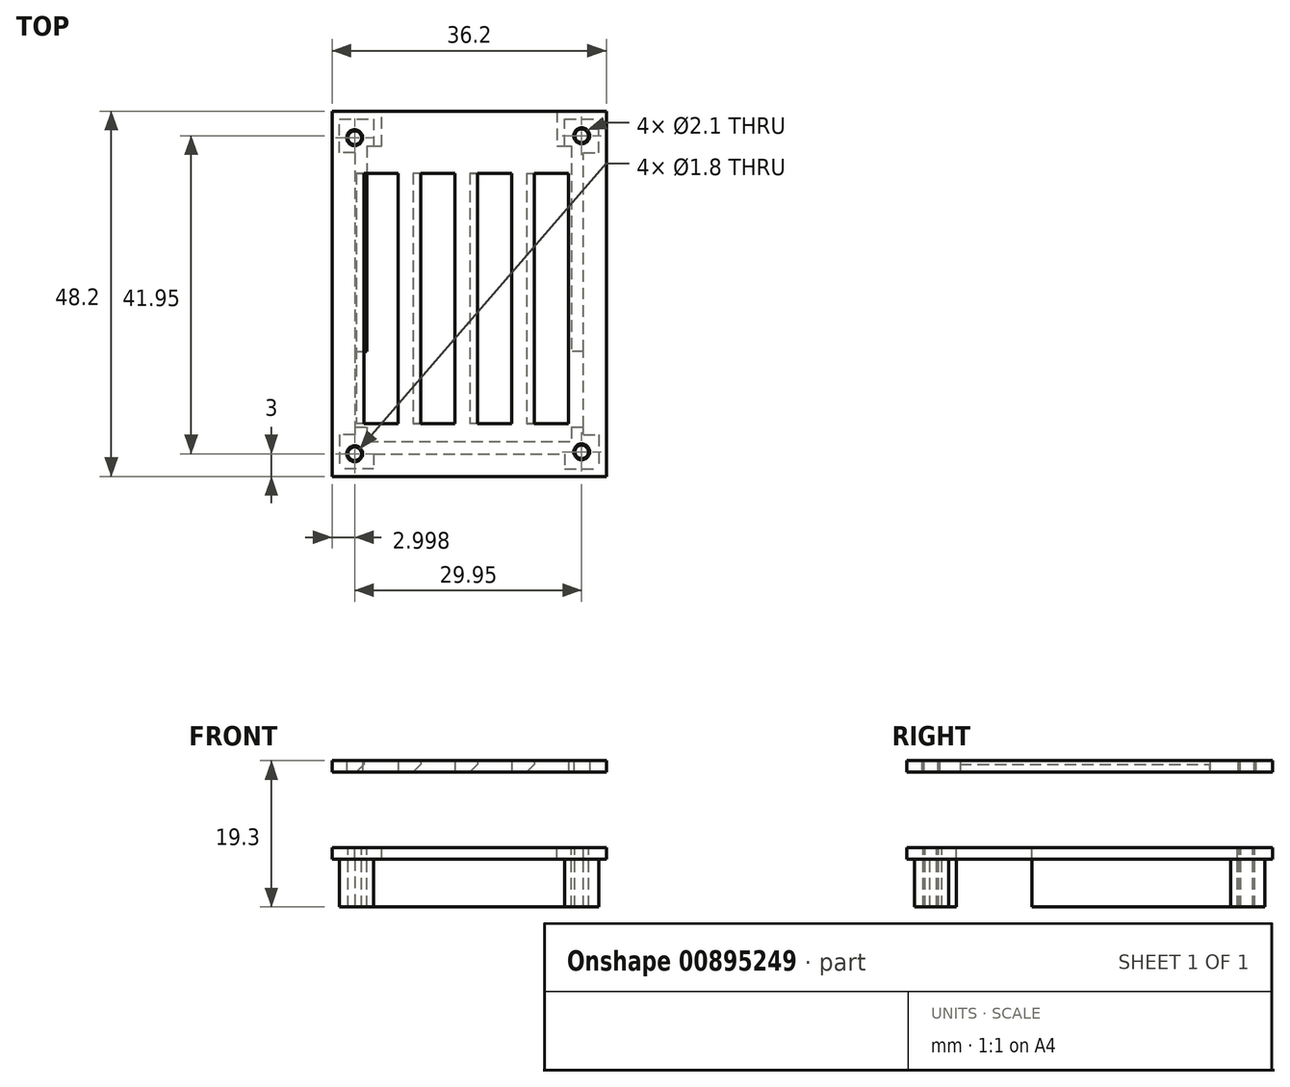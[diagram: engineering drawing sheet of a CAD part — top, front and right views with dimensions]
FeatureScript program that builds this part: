
annotation { "Feature Type Name" : "Feature", "Feature Type Description" : "" }
export const myFeature = defineFeature(function(context is Context, id is Id, definition is map)
    precondition{}
    {
        {
            var Q0;
            Q0=qCreatedBy(makeId("Top.planeOp"),FACE);
            var sketch = newSketch(context, id + "F0", { "sketchPlane" : qUnion([Q0])});
            skLineSegment(sketch, "E0.bottom", {"start": v(-14.17, 10.15) * mm, "end": v(12.83, 10.15) * mm});
            skLineSegment(sketch, "E0.top", {"start": v(-14.17, -28.85) * mm, "end": v(12.83, -28.85) * mm});
            skLineSegment(sketch, "E0.left", {"start": v(-14.17, 10.15) * mm, "end": v(-14.17, -28.85) * mm});
            skLineSegment(sketch, "E0.right", {"start": v(12.83, 10.15) * mm, "end": v(12.83, -28.85) * mm});
            skLineSegment(sketch, "E1.bottom", {"start": v(-12.17, 10.15) * mm, "end": v(-3.17, 10.15) * mm});
            skLineSegment(sketch, "E1.left", {"start": v(-12.17, 10.15) * mm, "end": v(-12.17, 14.75) * mm});
            skLineSegment(sketch, "E2", {"start": v(-15.77, 11.75) * mm, "end": v(-15.77, -30.45) * mm});
            skLineSegment(sketch, "E3", {"start": v(-15.77, -30.45) * mm, "end": v(14.43, -30.45) * mm});
            skLineSegment(sketch, "E4", {"start": v(14.43, -30.45) * mm, "end": v(14.43, 11.75) * mm});
            skLineSegment(sketch, "E5", {"start": v(14.43, 11.75) * mm, "end": v(10.93, 11.75) * mm});
            skLineSegment(sketch, "E6", {"start": v(-1.77, 31.75) * mm, "end": v(-3.27, 31.75) * mm});
            skLineSegment(sketch, "E7", {"start": v(-13.77, 14.75) * mm, "end": v(-13.77, 11.75) * mm});
            skLineSegment(sketch, "E8", {"start": v(-13.77, 11.75) * mm, "end": v(-15.77, 11.75) * mm});
            skLineSegment(sketch, "E9", {"start": v(-13.77, 14.75) * mm, "end": v(-18.77, 14.75) * mm});
            skLineSegment(sketch, "E10", {"start": v(-18.77, 14.75) * mm, "end": v(-18.77, -33.45) * mm});
            skLineSegment(sketch, "E11", {"start": v(-18.77, -33.45) * mm, "end": v(17.43, -33.45) * mm});
            skLineSegment(sketch, "E12", {"start": v(17.43, -33.45) * mm, "end": v(17.43, 14.75) * mm});
            skLineSegment(sketch, "E13", {"start": v(17.43, 14.75) * mm, "end": v(10.93, 14.75) * mm});
            skLineSegment(sketch, "E14.bottom", {"start": v(11.93, 9.25) * mm, "end": v(16.43, 9.25) * mm});
            skLineSegment(sketch, "E14.top", {"start": v(11.93, 13.75) * mm, "end": v(16.43, 13.75) * mm});
            skLineSegment(sketch, "E14.left", {"start": v(11.93, 9.25) * mm, "end": v(11.93, 13.75) * mm});
            skLineSegment(sketch, "E14.right", {"start": v(16.43, 9.25) * mm, "end": v(16.43, 13.75) * mm});
            skLineSegment(sketch, "E15.bottom", {"start": v(-13.27, 9.25) * mm, "end": v(-17.77, 9.25) * mm});
            skLineSegment(sketch, "E15.top", {"start": v(-13.27, 13.75) * mm, "end": v(-17.77, 13.75) * mm});
            skLineSegment(sketch, "E15.left", {"start": v(-13.27, 9.25) * mm, "end": v(-13.27, 13.75) * mm});
            skLineSegment(sketch, "E15.right", {"start": v(-17.77, 9.25) * mm, "end": v(-17.77, 13.75) * mm});
            skLineSegment(sketch, "E16.bottom", {"start": v(-13.27, -27.95) * mm, "end": v(-17.77, -27.95) * mm});
            skLineSegment(sketch, "E16.top", {"start": v(-13.27, -32.45) * mm, "end": v(-17.77, -32.45) * mm});
            skLineSegment(sketch, "E16.left", {"start": v(-13.27, -27.95) * mm, "end": v(-13.27, -32.45) * mm});
            skLineSegment(sketch, "E16.right", {"start": v(-17.77, -27.95) * mm, "end": v(-17.77, -32.45) * mm});
            skLineSegment(sketch, "E17.bottom", {"start": v(11.93, -27.95) * mm, "end": v(16.43, -27.95) * mm});
            skLineSegment(sketch, "E17.top", {"start": v(11.93, -32.45) * mm, "end": v(16.43, -32.45) * mm});
            skLineSegment(sketch, "E17.left", {"start": v(11.93, -27.95) * mm, "end": v(11.93, -32.45) * mm});
            skLineSegment(sketch, "E17.right", {"start": v(16.43, -27.95) * mm, "end": v(16.43, -32.45) * mm});
            skCircle(sketch, "E18", {"center": v(14.18, 11.5) * mm, "radius": 2.25 * mm});
            skPoint(sketch, "E18.centerSnap0", {"position": v(16.43, 11.5) * mm});
            skCircle(sketch, "E19", {"center": v(-15.77, 11.25) * mm, "radius": 2 * mm});
            skCircle(sketch, "E20", {"center": v(-15.77, -30.45) * mm, "radius": 2 * mm});
            skCircle(sketch, "E21", {"center": v(14.18, -30.2) * mm, "radius": 2.25 * mm});
            skLineSegment(sketch, "E22", {"start": v(-12.17, 30.25) * mm, "end": v(-12.17, 31.75) * mm});
            skLineSegment(sketch, "E23", {"start": v(-3.27, 30.25) * mm, "end": v(-3.27, 31.75) * mm});
            skLineSegment(sketch, "E24.trimOffspring", {"start": v(-12.17, 31.75) * mm, "end": v(-13.77, 31.75) * mm});
            skLineSegment(sketch, "E25", {"start": v(-13.77, 14.75) * mm, "end": v(-12.17, 14.75) * mm});
            skLineSegment(sketch, "E26", {"start": v(10.93, 14.75) * mm, "end": v(10.93, 10.15) * mm});
            skLineSegment(sketch, "E27", {"start": v(14.43, -16.95) * mm, "end": v(12.83, -16.95) * mm});
            skLineSegment(sketch, "E28", {"start": v(-13.27, 13.75) * mm, "end": v(-13.27, 14.75) * mm});
            skLineSegment(sketch, "E29", {"start": v(-15.77, -16.95) * mm, "end": v(-14.17, -16.95) * mm});
            skLineSegment(sketch, "E30", {"start": v(-15.77, -26.95) * mm, "end": v(-14.17, -26.95) * mm});
            skLineSegment(sketch, "E31", {"start": v(12.83, -26.95) * mm, "end": v(14.43, -26.95) * mm});
            skSolve(sketch);
        }
        {
            var Q0;
            Q0=makeQuery(id+"F0.imprint","IMPRINT",FACE,{"disambiguationData":[TD([[makeQuery(id+"F0.imprint","IMPRINT",EDGE,{"derivedFrom":sQuery(id+"F0.wireOp",EDGE,"E0.top")}),-1.0]])]});
            var Q1;
            {var subQ5=sQuery(id+"F0.wireOp",EDGE,"E0.left");var subQ6=sQuery(id+"F0.wireOp",EDGE,"E0.top");var subQ7=makeQuery(id+"F0.imprint","INTERSECT",VERTEX,{"derivedFrom":[subQ6,subQ5]});Q1=makeQuery(id+"F0.imprint","IMPRINT",FACE,{"disambiguationData":[TD([[makeQuery(id+"F0.imprint","IMPRINT",EDGE,{"disambiguationData":[TD([[subQ7,-1.0]])],"derivedFrom":subQ6}),-1.0]])]});}
            var Q2;
            {var subQ5=sQuery(id+"F0.wireOp",EDGE,"E0.right");var subQ6=sQuery(id+"F0.wireOp",EDGE,"E0.top");var subQ7=makeQuery(id+"F0.imprint","INTERSECT",VERTEX,{"derivedFrom":[subQ6,subQ5]});Q2=makeQuery(id+"F0.imprint","IMPRINT",FACE,{"disambiguationData":[TD([[makeQuery(id+"F0.imprint","IMPRINT",EDGE,{"disambiguationData":[TD([[subQ7,1.0]])],"derivedFrom":subQ6}),-1.0]])]});}
            var Q3;
            {var subQ0=sQuery(id+"F0.wireOp",EDGE,"E14.bottom");var subQ1=sQuery(id+"F0.wireOp",EDGE,"E0.right");var subQ2=makeQuery(id+"F0.imprint","INTERSECT",VERTEX,{"derivedFrom":[subQ1,subQ0]});Q3=makeQuery(id+"F0.imprint","IMPRINT",FACE,{"disambiguationData":[TD([[makeQuery(id+"F0.imprint","IMPRINT",EDGE,{"disambiguationData":[TD([[subQ2,-1.0]])],"derivedFrom":subQ1}),1.0]])]});}
            var Q4;
            {var subQ7=sQuery(id+"F0.wireOp",EDGE,"E0.right");var subQ8=sQuery(id+"F0.wireOp",EDGE,"E0.bottom");var subQ9=makeQuery(id+"F0.imprint","INTERSECT",VERTEX,{"derivedFrom":[subQ8,subQ7]});Q4=makeQuery(id+"F0.imprint","IMPRINT",FACE,{"disambiguationData":[TD([[makeQuery(id+"F0.imprint","IMPRINT",EDGE,{"disambiguationData":[TD([[subQ9,1.0]])],"derivedFrom":subQ8}),1.0]])]});}
            var Q5;
            {var subQ0=sQuery(id+"F0.wireOp",EDGE,"E15.bottom");var subQ1=sQuery(id+"F0.wireOp",EDGE,"E0.left");var subQ2=makeQuery(id+"F0.imprint","INTERSECT",VERTEX,{"derivedFrom":[subQ1,subQ0]});Q5=makeQuery(id+"F0.imprint","IMPRINT",FACE,{"disambiguationData":[TD([[makeQuery(id+"F0.imprint","IMPRINT",EDGE,{"disambiguationData":[TD([[subQ2,-1.0]])],"derivedFrom":subQ1}),-1.0]])]});}
            var Q6;
            {var subQ0=sQuery(id+"F0.wireOp",EDGE,"E16.bottom");var subQ1=sQuery(id+"F0.wireOp",EDGE,"E0.left");var subQ2=makeQuery(id+"F0.imprint","INTERSECT",VERTEX,{"derivedFrom":[subQ1,subQ0]});Q6=makeQuery(id+"F0.imprint","IMPRINT",FACE,{"disambiguationData":[TD([[makeQuery(id+"F0.imprint","IMPRINT",EDGE,{"disambiguationData":[TD([[subQ2,-1.0]])],"derivedFrom":subQ1}),-1.0]])]});}
            var Q7;
            {var subQ0=sQuery(id+"F0.wireOp",EDGE,"E20");var subQ1=sQuery(id+"F0.wireOp",EDGE,"E3");var subQ2=makeQuery(id+"F0.imprint","INTERSECT",VERTEX,{"derivedFrom":[subQ1,subQ0]});Q7=makeQuery(id+"F0.imprint","IMPRINT",FACE,{"disambiguationData":[TD([[makeQuery(id+"F0.imprint","IMPRINT",EDGE,{"disambiguationData":[TD([[subQ2,-1.0]])],"derivedFrom":subQ1}),1.0]])]});}
            var Q8;
            {var subQ0=sQuery(id+"F0.wireOp",EDGE,"E16.left");var subQ1=sQuery(id+"F0.wireOp",EDGE,"E0.top");var subQ2=makeQuery(id+"F0.imprint","INTERSECT",VERTEX,{"derivedFrom":[subQ1,subQ0]});Q8=makeQuery(id+"F0.imprint","IMPRINT",FACE,{"disambiguationData":[TD([[makeQuery(id+"F0.imprint","IMPRINT",EDGE,{"disambiguationData":[TD([[subQ2,-1.0]])],"derivedFrom":subQ1}),-1.0]])]});}
            var Q9;
            {var subQ0=sQuery(id+"F0.wireOp",EDGE,"E16.bottom");var subQ1=sQuery(id+"F0.wireOp",EDGE,"E2");var subQ2=makeQuery(id+"F0.imprint","INTERSECT",VERTEX,{"derivedFrom":[subQ1,subQ0]});Q9=makeQuery(id+"F0.imprint","IMPRINT",FACE,{"disambiguationData":[TD([[makeQuery(id+"F0.imprint","IMPRINT",EDGE,{"disambiguationData":[TD([[subQ2,-1.0]])],"derivedFrom":subQ1}),1.0]])]});}
            var Q10;
            {var subQ0=sQuery(id+"F0.wireOp",EDGE,"E17.bottom");var subQ1=sQuery(id+"F0.wireOp",EDGE,"E0.right");var subQ2=makeQuery(id+"F0.imprint","INTERSECT",VERTEX,{"derivedFrom":[subQ1,subQ0]});Q10=makeQuery(id+"F0.imprint","IMPRINT",FACE,{"disambiguationData":[TD([[makeQuery(id+"F0.imprint","IMPRINT",EDGE,{"disambiguationData":[TD([[subQ2,-1.0]])],"derivedFrom":subQ1}),1.0]])]});}
            var Q11;
            {var subQ0=sQuery(id+"F0.wireOp",EDGE,"E17.left");var subQ1=sQuery(id+"F0.wireOp",EDGE,"E3");var subQ2=makeQuery(id+"F0.imprint","INTERSECT",VERTEX,{"derivedFrom":[subQ1,subQ0]});Q11=makeQuery(id+"F0.imprint","IMPRINT",FACE,{"disambiguationData":[TD([[makeQuery(id+"F0.imprint","IMPRINT",EDGE,{"disambiguationData":[TD([[subQ2,-1.0]])],"derivedFrom":subQ1}),1.0]])]});}
            var Q12;
            {var subQ0=sQuery(id+"F0.wireOp",EDGE,"E21");var subQ1=sQuery(id+"F0.wireOp",EDGE,"E4");var subQ2=makeQuery(id+"F0.imprint","INTERSECT",VERTEX,{"derivedFrom":[subQ1,subQ0]});Q12=makeQuery(id+"F0.imprint","IMPRINT",FACE,{"disambiguationData":[TD([[makeQuery(id+"F0.imprint","IMPRINT",EDGE,{"disambiguationData":[TD([[subQ2,-1.0]])],"derivedFrom":subQ1}),1.0]])]});}
            var Q13;
            {var subQ0=sQuery(id+"F0.wireOp",EDGE,"E14.left");var subQ1=sQuery(id+"F0.wireOp",EDGE,"E0.bottom");var subQ2=makeQuery(id+"F0.imprint","INTERSECT",VERTEX,{"derivedFrom":[subQ1,subQ0]});Q13=makeQuery(id+"F0.imprint","IMPRINT",FACE,{"disambiguationData":[TD([[makeQuery(id+"F0.imprint","IMPRINT",EDGE,{"disambiguationData":[TD([[subQ2,-1.0]])],"derivedFrom":subQ1}),1.0]])]});}
            var Q14;
            {var subQ0=sQuery(id+"F0.wireOp",EDGE,"E18");var subQ1=sQuery(id+"F0.wireOp",EDGE,"E5");var subQ2=makeQuery(id+"F0.imprint","INTERSECT",VERTEX,{"derivedFrom":[subQ1,subQ0]});Q14=makeQuery(id+"F0.imprint","IMPRINT",FACE,{"disambiguationData":[TD([[makeQuery(id+"F0.imprint","IMPRINT",EDGE,{"disambiguationData":[TD([[subQ2,-1.0]])],"derivedFrom":subQ1}),1.0]])]});}
            var Q15;
            {var subQ0=sQuery(id+"F0.wireOp",EDGE,"E14.bottom");var subQ1=sQuery(id+"F0.wireOp",EDGE,"E4");var subQ2=makeQuery(id+"F0.imprint","INTERSECT",VERTEX,{"derivedFrom":[subQ1,subQ0]});Q15=makeQuery(id+"F0.imprint","IMPRINT",FACE,{"disambiguationData":[TD([[makeQuery(id+"F0.imprint","IMPRINT",EDGE,{"disambiguationData":[TD([[subQ2,-1.0]])],"derivedFrom":subQ1}),1.0]])]});}
            var Q16;
            {var subQ0=sQuery(id+"F0.wireOp",EDGE,"E18");var subQ1=sQuery(id+"F0.wireOp",EDGE,"E0.right");var subQ2=makeQuery(id+"F0.imprint","INTERSECT",VERTEX,{"derivedFrom":[subQ1,subQ0]});Q16=makeQuery(id+"F0.imprint","IMPRINT",FACE,{"disambiguationData":[TD([[makeQuery(id+"F0.imprint","IMPRINT",EDGE,{"disambiguationData":[TD([[subQ2,-1.0]])],"derivedFrom":subQ1}),1.0]])]});}
            var Q17;
            {var subQ0=sQuery(id+"F0.wireOp",EDGE,"E15.top");var subQ1=sQuery(id+"F0.wireOp",EDGE,"E7");var subQ2=makeQuery(id+"F0.imprint","INTERSECT",VERTEX,{"derivedFrom":[subQ1,subQ0]});Q17=makeQuery(id+"F0.imprint","IMPRINT",FACE,{"disambiguationData":[TD([[makeQuery(id+"F0.imprint","IMPRINT",EDGE,{"disambiguationData":[TD([[subQ2,-1.0]])],"derivedFrom":subQ1}),1.0]])]});}
            var Q18;
            {var subQ0=sQuery(id+"F0.wireOp",EDGE,"E19");var subQ1=sQuery(id+"F0.wireOp",EDGE,"E2");var subQ2=makeQuery(id+"F0.imprint","INTERSECT",VERTEX,{"derivedFrom":[subQ1,subQ0]});Q18=makeQuery(id+"F0.imprint","IMPRINT",FACE,{"disambiguationData":[TD([[makeQuery(id+"F0.imprint","IMPRINT",EDGE,{"disambiguationData":[TD([[subQ2,-1.0]])],"derivedFrom":subQ1}),1.0]])]});}
            var Q19;
            {var subQ0=sQuery(id+"F0.wireOp",EDGE,"E19");var subQ1=sQuery(id+"F0.wireOp",EDGE,"E0.left");var subQ2=makeQuery(id+"F0.imprint","INTERSECT",VERTEX,{"derivedFrom":[subQ1,subQ0]});Q19=makeQuery(id+"F0.imprint","IMPRINT",FACE,{"disambiguationData":[TD([[makeQuery(id+"F0.imprint","IMPRINT",EDGE,{"disambiguationData":[TD([[subQ2,-1.0]])],"derivedFrom":subQ1}),-1.0]])]});}
            var Q20;
            {var subQ0=sQuery(id+"F0.wireOp",EDGE,"E19");var subQ1=sQuery(id+"F0.wireOp",EDGE,"E0.bottom");var subQ2=makeQuery(id+"F0.imprint","INTERSECT",VERTEX,{"derivedFrom":[subQ1,subQ0]});Q20=makeQuery(id+"F0.imprint","IMPRINT",FACE,{"disambiguationData":[TD([[makeQuery(id+"F0.imprint","IMPRINT",EDGE,{"disambiguationData":[TD([[subQ2,-1.0]])],"derivedFrom":subQ1}),1.0]])]});}
            var Q21;
            {var subQ0=sQuery(id+"F0.wireOp",EDGE,"E8");Q21=makeQuery(id+"F0.imprint","IMPRINT",FACE,{"disambiguationData":[TD([[makeQuery(id+"F0.imprint","IMPRINT",EDGE,{"derivedFrom":subQ0}),1.0]])]});}
            var Q22;
            {var subQ0=sQuery(id+"F0.wireOp",EDGE,"E3");var subQ1=sQuery(id+"F0.wireOp",EDGE,"E2");var subQ2=makeQuery(id+"F0.imprint","INTERSECT",VERTEX,{"derivedFrom":[subQ1,subQ0]});Q22=makeQuery(id+"F0.imprint","IMPRINT",FACE,{"disambiguationData":[TD([[makeQuery(id+"F0.imprint","IMPRINT",EDGE,{"disambiguationData":[TD([[subQ2,1.0]])],"derivedFrom":subQ1}),1.0]])]});}
            var Q23;
            {var subQ9=sQuery(id+"F0.wireOp",EDGE,"E1.right");Q23=makeQuery(id+"F0.imprint","IMPRINT",FACE,{"disambiguationData":[TD([[makeQuery(id+"F0.imprint","IMPRINT",EDGE,{"derivedFrom":subQ9}),-1.0]])]});}
            var Q24;
            {var subQ0=sQuery(id+"F0.wireOp",EDGE,"E30");Q24=makeQuery(id+"F0.imprint","IMPRINT",FACE,{"disambiguationData":[TD([[makeQuery(id+"F0.imprint","IMPRINT",EDGE,{"derivedFrom":subQ0}),-1.0]])]});}
            var Q25;
            {var subQ4=sQuery(id+"F0.wireOp",EDGE,"E31");Q25=makeQuery(id+"F0.imprint","IMPRINT",FACE,{"disambiguationData":[TD([[makeQuery(id+"F0.imprint","IMPRINT",EDGE,{"derivedFrom":subQ4}),-1.0]])]});}
            extrude(context, id + "F1", {"entities" : qUnion([Q0, Q1, Q2, Q3, Q4, Q5, Q6, Q7, Q8, Q9, Q10, Q11, Q12, Q13, Q14, Q15, Q16, Q17, Q18, Q19, Q20, Q21, Q22, Q23, Q24, Q25]), "oppositeDirection" : true, "depth" : 7.8 * mm, "offsetDistance" : 25 * mm});
        }
        {
            var Q0;
            {var subQ28=sQuery(id+"F0.wireOp",EDGE,"E9");Q0=makeQuery(id+"F0.imprint","IMPRINT",FACE,{"disambiguationData":[TD([[makeQuery(id+"F0.imprint","IMPRINT",EDGE,{"derivedFrom":subQ28}),1.0]])]});}
            var Q1;
            {var subQ5=sQuery(id+"F0.wireOp",EDGE,"E7");var subQ7=sQuery(id+"F0.wireOp",EDGE,"E8");var subQ8=makeQuery(id+"F0.imprint","INTERSECT",VERTEX,{"derivedFrom":[subQ5,subQ7]});Q1=makeQuery(id+"F0.imprint","IMPRINT",FACE,{"disambiguationData":[TD([[makeQuery(id+"F0.imprint","IMPRINT",EDGE,{"disambiguationData":[TD([[subQ8,1.0]])],"derivedFrom":subQ5}),-1.0]])]});}
            var Q2;
            {var subQ0=sQuery(id+"F0.wireOp",EDGE,"E8");var subQ1=sQuery(id+"F0.wireOp",EDGE,"E2");var subQ2=makeQuery(id+"F0.imprint","INTERSECT",VERTEX,{"derivedFrom":[subQ1,subQ0]});Q2=makeQuery(id+"F0.imprint","IMPRINT",FACE,{"disambiguationData":[TD([[makeQuery(id+"F0.imprint","IMPRINT",EDGE,{"disambiguationData":[TD([[subQ2,1.0]])],"derivedFrom":subQ0}),-1.0]])]});}
            var Q3;
            {var subQ0=sQuery(id+"F0.wireOp",EDGE,"E15.right");var subQ1=sQuery(id+"F0.wireOp",EDGE,"E15.bottom");var subQ2=makeQuery(id+"F0.imprint","INTERSECT",VERTEX,{"derivedFrom":[subQ1,subQ0]});Q3=makeQuery(id+"F0.imprint","IMPRINT",FACE,{"disambiguationData":[TD([[makeQuery(id+"F0.imprint","IMPRINT",EDGE,{"disambiguationData":[TD([[subQ2,-1.0]])],"derivedFrom":subQ0}),-1.0]])]});}
            var Q4;
            {var subQ0=sQuery(id+"F0.wireOp",EDGE,"E14.bottom");var subQ1=sQuery(id+"F0.wireOp",EDGE,"E4");var subQ2=makeQuery(id+"F0.imprint","INTERSECT",VERTEX,{"derivedFrom":[subQ1,subQ0]});Q4=makeQuery(id+"F0.imprint","IMPRINT",FACE,{"disambiguationData":[TD([[makeQuery(id+"F0.imprint","IMPRINT",EDGE,{"disambiguationData":[TD([[subQ2,-1.0]])],"derivedFrom":subQ1}),-1.0]])]});}
            var Q5;
            {var subQ1=sQuery(id+"F0.wireOp",EDGE,"E5");var subQ4=sQuery(id+"F0.wireOp",EDGE,"E4");var subQ5=makeQuery(id+"F0.imprint","INTERSECT",VERTEX,{"derivedFrom":[subQ4,subQ1]});Q5=makeQuery(id+"F0.imprint","IMPRINT",FACE,{"disambiguationData":[TD([[makeQuery(id+"F0.imprint","IMPRINT",EDGE,{"disambiguationData":[TD([[subQ5,1.0]])],"derivedFrom":subQ4}),-1.0]])]});}
            var Q6;
            {var subQ0=sQuery(id+"F0.wireOp",EDGE,"E14.right");var subQ1=sQuery(id+"F0.wireOp",EDGE,"E14.top");var subQ2=makeQuery(id+"F0.imprint","INTERSECT",VERTEX,{"derivedFrom":[subQ1,subQ0]});Q6=makeQuery(id+"F0.imprint","IMPRINT",FACE,{"disambiguationData":[TD([[makeQuery(id+"F0.imprint","IMPRINT",EDGE,{"disambiguationData":[TD([[subQ2,1.0]])],"derivedFrom":subQ1}),-1.0]])]});}
            var Q7;
            {var subQ0=sQuery(id+"F0.wireOp",EDGE,"E18");var subQ1=sQuery(id+"F0.wireOp",EDGE,"E5");var subQ2=makeQuery(id+"F0.imprint","INTERSECT",VERTEX,{"derivedFrom":[subQ1,subQ0]});Q7=makeQuery(id+"F0.imprint","IMPRINT",FACE,{"disambiguationData":[TD([[makeQuery(id+"F0.imprint","IMPRINT",EDGE,{"disambiguationData":[TD([[subQ2,-1.0]])],"derivedFrom":subQ1}),-1.0]])]});}
            var Q8;
            {var subQ0=sQuery(id+"F0.wireOp",EDGE,"E20");var subQ1=sQuery(id+"F0.wireOp",EDGE,"E3");var subQ2=makeQuery(id+"F0.imprint","INTERSECT",VERTEX,{"derivedFrom":[subQ1,subQ0]});Q8=makeQuery(id+"F0.imprint","IMPRINT",FACE,{"disambiguationData":[TD([[makeQuery(id+"F0.imprint","IMPRINT",EDGE,{"disambiguationData":[TD([[subQ2,-1.0]])],"derivedFrom":subQ1}),-1.0]])]});}
            var Q9;
            {var subQ1=sQuery(id+"F0.wireOp",EDGE,"E2");var subQ4=sQuery(id+"F0.wireOp",EDGE,"E3");var subQ5=makeQuery(id+"F0.imprint","INTERSECT",VERTEX,{"derivedFrom":[subQ1,subQ4]});Q9=makeQuery(id+"F0.imprint","IMPRINT",FACE,{"disambiguationData":[TD([[makeQuery(id+"F0.imprint","IMPRINT",EDGE,{"disambiguationData":[TD([[subQ5,1.0]])],"derivedFrom":subQ1}),-1.0]])]});}
            var Q10;
            {var subQ0=sQuery(id+"F0.wireOp",EDGE,"E16.right");var subQ1=sQuery(id+"F0.wireOp",EDGE,"E16.top");var subQ2=makeQuery(id+"F0.imprint","INTERSECT",VERTEX,{"derivedFrom":[subQ1,subQ0]});Q10=makeQuery(id+"F0.imprint","IMPRINT",FACE,{"disambiguationData":[TD([[makeQuery(id+"F0.imprint","IMPRINT",EDGE,{"disambiguationData":[TD([[subQ2,1.0]])],"derivedFrom":subQ1}),-1.0]])]});}
            var Q11;
            {var subQ0=sQuery(id+"F0.wireOp",EDGE,"E16.bottom");var subQ1=sQuery(id+"F0.wireOp",EDGE,"E2");var subQ2=makeQuery(id+"F0.imprint","INTERSECT",VERTEX,{"derivedFrom":[subQ1,subQ0]});Q11=makeQuery(id+"F0.imprint","IMPRINT",FACE,{"disambiguationData":[TD([[makeQuery(id+"F0.imprint","IMPRINT",EDGE,{"disambiguationData":[TD([[subQ2,-1.0]])],"derivedFrom":subQ1}),-1.0]])]});}
            var Q12;
            {var subQ0=sQuery(id+"F0.wireOp",EDGE,"E21");var subQ1=sQuery(id+"F0.wireOp",EDGE,"E4");var subQ2=makeQuery(id+"F0.imprint","INTERSECT",VERTEX,{"derivedFrom":[subQ1,subQ0]});Q12=makeQuery(id+"F0.imprint","IMPRINT",FACE,{"disambiguationData":[TD([[makeQuery(id+"F0.imprint","IMPRINT",EDGE,{"disambiguationData":[TD([[subQ2,-1.0]])],"derivedFrom":subQ1}),-1.0]])]});}
            var Q13;
            {var subQ1=sQuery(id+"F0.wireOp",EDGE,"E3");var subQ4=sQuery(id+"F0.wireOp",EDGE,"E4");var subQ5=makeQuery(id+"F0.imprint","INTERSECT",VERTEX,{"derivedFrom":[subQ1,subQ4]});Q13=makeQuery(id+"F0.imprint","IMPRINT",FACE,{"disambiguationData":[TD([[makeQuery(id+"F0.imprint","IMPRINT",EDGE,{"disambiguationData":[TD([[subQ5,1.0]])],"derivedFrom":subQ1}),-1.0]])]});}
            var Q14;
            {var subQ0=sQuery(id+"F0.wireOp",EDGE,"E17.right");var subQ1=sQuery(id+"F0.wireOp",EDGE,"E17.top");var subQ2=makeQuery(id+"F0.imprint","INTERSECT",VERTEX,{"derivedFrom":[subQ1,subQ0]});Q14=makeQuery(id+"F0.imprint","IMPRINT",FACE,{"disambiguationData":[TD([[makeQuery(id+"F0.imprint","IMPRINT",EDGE,{"disambiguationData":[TD([[subQ2,1.0]])],"derivedFrom":subQ1}),1.0]])]});}
            var Q15;
            {var subQ0=sQuery(id+"F0.wireOp",EDGE,"E17.left");var subQ1=sQuery(id+"F0.wireOp",EDGE,"E3");var subQ2=makeQuery(id+"F0.imprint","INTERSECT",VERTEX,{"derivedFrom":[subQ1,subQ0]});Q15=makeQuery(id+"F0.imprint","IMPRINT",FACE,{"disambiguationData":[TD([[makeQuery(id+"F0.imprint","IMPRINT",EDGE,{"disambiguationData":[TD([[subQ2,-1.0]])],"derivedFrom":subQ1}),-1.0]])]});}
            var Q16;
            {var subQ5=sQuery(id+"F0.wireOp",EDGE,"E28");Q16=makeQuery(id+"F0.imprint","IMPRINT",FACE,{"disambiguationData":[TD([[makeQuery(id+"F0.imprint","IMPRINT",EDGE,{"derivedFrom":subQ5}),1.0]])]});}
            var Q17;
            {var subQ7=sQuery(id+"F0.wireOp",EDGE,"E19");var subQ9=sQuery(id+"F0.wireOp",EDGE,"E0.bottom");var subQ10=makeQuery(id+"F0.imprint","INTERSECT",VERTEX,{"derivedFrom":[subQ9,subQ7]});Q17=makeQuery(id+"F0.imprint","IMPRINT",FACE,{"disambiguationData":[TD([[makeQuery(id+"F0.imprint","IMPRINT",EDGE,{"disambiguationData":[TD([[subQ10,-1.0]])],"derivedFrom":subQ9}),1.0]])]});}
            var Q18;
            {var subQ1=sQuery(id+"F0.wireOp",EDGE,"E1.left");Q18=makeQuery(id+"F0.imprint","IMPRINT",FACE,{"disambiguationData":[TD([[makeQuery(id+"F0.imprint","IMPRINT",EDGE,{"derivedFrom":subQ1}),1.0]])]});}
            var Q19;
            {var subQ4=sQuery(id+"F0.wireOp",EDGE,"E0.bottom");var subQ6=sQuery(id+"F0.wireOp",EDGE,"E26");var subQ8=makeQuery(id+"F0.imprint","INTERSECT",VERTEX,{"derivedFrom":[subQ4,subQ6]});Q19=makeQuery(id+"F0.imprint","IMPRINT",FACE,{"disambiguationData":[TD([[makeQuery(id+"F0.imprint","IMPRINT",EDGE,{"disambiguationData":[TD([[subQ8,-1.0]])],"derivedFrom":subQ4}),1.0]])]});}
            extrude(context, id + "F2", {"entities" : qUnion([Q0, Q1, Q2, Q3, Q4, Q5, Q6, Q7, Q8, Q9, Q10, Q11, Q12, Q13, Q14, Q15, Q16, Q17, Q18, Q19]), "operationType" : NewBodyOperationType.ADD, "oppositeDirection" : true, "depth" : 1.5 * mm, "offsetDistance" : 25 * mm});
        }
        {
            var Q0;
            {var subQ1=sQuery(id+"F0.wireOp",EDGE,"E5");var subQ4=sQuery(id+"F0.wireOp",EDGE,"E4");var subQ5=makeQuery(id+"F0.imprint","INTERSECT",VERTEX,{"derivedFrom":[subQ4,subQ1]});Q0=makeQuery(id+"F0.imprint","IMPRINT",FACE,{"disambiguationData":[TD([[makeQuery(id+"F0.imprint","IMPRINT",EDGE,{"disambiguationData":[TD([[subQ5,1.0]])],"derivedFrom":subQ4}),-1.0]])]});}
            var Q1;
            {var subQ0=sQuery(id+"F0.wireOp",EDGE,"E18");var subQ1=sQuery(id+"F0.wireOp",EDGE,"E0.right");var subQ2=makeQuery(id+"F0.imprint","INTERSECT",VERTEX,{"derivedFrom":[subQ1,subQ0]});Q1=makeQuery(id+"F0.imprint","IMPRINT",FACE,{"disambiguationData":[TD([[makeQuery(id+"F0.imprint","IMPRINT",EDGE,{"disambiguationData":[TD([[subQ2,-1.0]])],"derivedFrom":subQ1}),1.0]])]});}
            var Q2;
            {var subQ0=sQuery(id+"F0.wireOp",EDGE,"E18");var subQ1=sQuery(id+"F0.wireOp",EDGE,"E5");var subQ2=makeQuery(id+"F0.imprint","INTERSECT",VERTEX,{"derivedFrom":[subQ1,subQ0]});Q2=makeQuery(id+"F0.imprint","IMPRINT",FACE,{"disambiguationData":[TD([[makeQuery(id+"F0.imprint","IMPRINT",EDGE,{"disambiguationData":[TD([[subQ2,-1.0]])],"derivedFrom":subQ1}),-1.0]])]});}
            var Q3;
            {var subQ6=sQuery(id+"F0.wireOp",EDGE,"E0.right");var subQ7=sQuery(id+"F0.wireOp",EDGE,"E0.bottom");var subQ8=makeQuery(id+"F0.imprint","INTERSECT",VERTEX,{"derivedFrom":[subQ7,subQ6]});Q3=makeQuery(id+"F0.imprint","IMPRINT",FACE,{"disambiguationData":[TD([[makeQuery(id+"F0.imprint","IMPRINT",EDGE,{"disambiguationData":[TD([[subQ8,1.0]])],"derivedFrom":subQ7}),1.0]])]});}
            var Q4;
            {var subQ0=sQuery(id+"F0.wireOp",EDGE,"E14.left");var subQ1=sQuery(id+"F0.wireOp",EDGE,"E0.bottom");var subQ2=makeQuery(id+"F0.imprint","INTERSECT",VERTEX,{"derivedFrom":[subQ1,subQ0]});Q4=makeQuery(id+"F0.imprint","IMPRINT",FACE,{"disambiguationData":[TD([[makeQuery(id+"F0.imprint","IMPRINT",EDGE,{"disambiguationData":[TD([[subQ2,-1.0]])],"derivedFrom":subQ1}),1.0]])]});}
            var Q5;
            {var subQ6=sQuery(id+"F0.wireOp",EDGE,"E0.left");var subQ7=sQuery(id+"F0.wireOp",EDGE,"E0.bottom");var subQ8=makeQuery(id+"F0.imprint","INTERSECT",VERTEX,{"derivedFrom":[subQ7,subQ6]});Q5=makeQuery(id+"F0.imprint","IMPRINT",FACE,{"disambiguationData":[TD([[makeQuery(id+"F0.imprint","IMPRINT",EDGE,{"disambiguationData":[TD([[subQ8,-1.0]])],"derivedFrom":subQ7}),1.0]])]});}
            var Q6;
            {var subQ0=sQuery(id+"F0.wireOp",EDGE,"E8");var subQ1=sQuery(id+"F0.wireOp",EDGE,"E2");var subQ2=makeQuery(id+"F0.imprint","INTERSECT",VERTEX,{"derivedFrom":[subQ1,subQ0]});Q6=makeQuery(id+"F0.imprint","IMPRINT",FACE,{"disambiguationData":[TD([[makeQuery(id+"F0.imprint","IMPRINT",EDGE,{"disambiguationData":[TD([[subQ2,1.0]])],"derivedFrom":subQ0}),-1.0]])]});}
            var Q7;
            {var subQ5=sQuery(id+"F0.wireOp",EDGE,"E7");var subQ7=sQuery(id+"F0.wireOp",EDGE,"E8");var subQ8=makeQuery(id+"F0.imprint","INTERSECT",VERTEX,{"derivedFrom":[subQ5,subQ7]});Q7=makeQuery(id+"F0.imprint","IMPRINT",FACE,{"disambiguationData":[TD([[makeQuery(id+"F0.imprint","IMPRINT",EDGE,{"disambiguationData":[TD([[subQ8,1.0]])],"derivedFrom":subQ5}),-1.0]])]});}
            var Q8;
            {var subQ0=sQuery(id+"F0.wireOp",EDGE,"E15.right");var subQ1=sQuery(id+"F0.wireOp",EDGE,"E15.bottom");var subQ2=makeQuery(id+"F0.imprint","INTERSECT",VERTEX,{"derivedFrom":[subQ1,subQ0]});Q8=makeQuery(id+"F0.imprint","IMPRINT",FACE,{"disambiguationData":[TD([[makeQuery(id+"F0.imprint","IMPRINT",EDGE,{"disambiguationData":[TD([[subQ2,-1.0]])],"derivedFrom":subQ0}),-1.0]])]});}
            var Q9;
            {var subQ0=sQuery(id+"F0.wireOp",EDGE,"E19");var subQ1=sQuery(id+"F0.wireOp",EDGE,"E0.left");var subQ2=makeQuery(id+"F0.imprint","INTERSECT",VERTEX,{"derivedFrom":[subQ1,subQ0]});Q9=makeQuery(id+"F0.imprint","IMPRINT",FACE,{"disambiguationData":[TD([[makeQuery(id+"F0.imprint","IMPRINT",EDGE,{"disambiguationData":[TD([[subQ2,-1.0]])],"derivedFrom":subQ1}),-1.0]])]});}
            var Q10;
            {var subQ7=sQuery(id+"F0.wireOp",EDGE,"E19");var subQ9=sQuery(id+"F0.wireOp",EDGE,"E0.bottom");var subQ10=makeQuery(id+"F0.imprint","INTERSECT",VERTEX,{"derivedFrom":[subQ9,subQ7]});Q10=makeQuery(id+"F0.imprint","IMPRINT",FACE,{"disambiguationData":[TD([[makeQuery(id+"F0.imprint","IMPRINT",EDGE,{"disambiguationData":[TD([[subQ10,-1.0]])],"derivedFrom":subQ9}),1.0]])]});}
            var Q11;
            {var subQ0=sQuery(id+"F0.wireOp",EDGE,"E14.right");var subQ1=sQuery(id+"F0.wireOp",EDGE,"E14.top");var subQ2=makeQuery(id+"F0.imprint","INTERSECT",VERTEX,{"derivedFrom":[subQ1,subQ0]});Q11=makeQuery(id+"F0.imprint","IMPRINT",FACE,{"disambiguationData":[TD([[makeQuery(id+"F0.imprint","IMPRINT",EDGE,{"disambiguationData":[TD([[subQ2,1.0]])],"derivedFrom":subQ1}),-1.0]])]});}
            var Q12;
            {var subQ0=sQuery(id+"F0.wireOp",EDGE,"E14.bottom");var subQ1=sQuery(id+"F0.wireOp",EDGE,"E4");var subQ2=makeQuery(id+"F0.imprint","INTERSECT",VERTEX,{"derivedFrom":[subQ1,subQ0]});Q12=makeQuery(id+"F0.imprint","IMPRINT",FACE,{"disambiguationData":[TD([[makeQuery(id+"F0.imprint","IMPRINT",EDGE,{"disambiguationData":[TD([[subQ2,-1.0]])],"derivedFrom":subQ1}),-1.0]])]});}
            var Q13;
            {var subQ1=sQuery(id+"F0.wireOp",EDGE,"E3");var subQ4=sQuery(id+"F0.wireOp",EDGE,"E4");var subQ5=makeQuery(id+"F0.imprint","INTERSECT",VERTEX,{"derivedFrom":[subQ1,subQ4]});Q13=makeQuery(id+"F0.imprint","IMPRINT",FACE,{"disambiguationData":[TD([[makeQuery(id+"F0.imprint","IMPRINT",EDGE,{"disambiguationData":[TD([[subQ5,1.0]])],"derivedFrom":subQ1}),-1.0]])]});}
            var Q14;
            {var subQ0=sQuery(id+"F0.wireOp",EDGE,"E21");var subQ1=sQuery(id+"F0.wireOp",EDGE,"E4");var subQ2=makeQuery(id+"F0.imprint","INTERSECT",VERTEX,{"derivedFrom":[subQ1,subQ0]});Q14=makeQuery(id+"F0.imprint","IMPRINT",FACE,{"disambiguationData":[TD([[makeQuery(id+"F0.imprint","IMPRINT",EDGE,{"disambiguationData":[TD([[subQ2,-1.0]])],"derivedFrom":subQ1}),-1.0]])]});}
            var Q15;
            {var subQ0=sQuery(id+"F0.wireOp",EDGE,"E17.right");var subQ1=sQuery(id+"F0.wireOp",EDGE,"E17.top");var subQ2=makeQuery(id+"F0.imprint","INTERSECT",VERTEX,{"derivedFrom":[subQ1,subQ0]});Q15=makeQuery(id+"F0.imprint","IMPRINT",FACE,{"disambiguationData":[TD([[makeQuery(id+"F0.imprint","IMPRINT",EDGE,{"disambiguationData":[TD([[subQ2,1.0]])],"derivedFrom":subQ1}),1.0]])]});}
            var Q16;
            {var subQ0=sQuery(id+"F0.wireOp",EDGE,"E17.left");var subQ1=sQuery(id+"F0.wireOp",EDGE,"E3");var subQ2=makeQuery(id+"F0.imprint","INTERSECT",VERTEX,{"derivedFrom":[subQ1,subQ0]});Q16=makeQuery(id+"F0.imprint","IMPRINT",FACE,{"disambiguationData":[TD([[makeQuery(id+"F0.imprint","IMPRINT",EDGE,{"disambiguationData":[TD([[subQ2,-1.0]])],"derivedFrom":subQ1}),-1.0]])]});}
            var Q17;
            {var subQ6=sQuery(id+"F0.wireOp",EDGE,"E0.right");var subQ7=sQuery(id+"F0.wireOp",EDGE,"E0.top");var subQ8=makeQuery(id+"F0.imprint","INTERSECT",VERTEX,{"derivedFrom":[subQ7,subQ6]});Q17=makeQuery(id+"F0.imprint","IMPRINT",FACE,{"disambiguationData":[TD([[makeQuery(id+"F0.imprint","IMPRINT",EDGE,{"disambiguationData":[TD([[subQ8,1.0]])],"derivedFrom":subQ7}),-1.0]])]});}
            var Q18;
            {var subQ0=sQuery(id+"F0.wireOp",EDGE,"E17.left");var subQ1=sQuery(id+"F0.wireOp",EDGE,"E0.top");var subQ2=makeQuery(id+"F0.imprint","INTERSECT",VERTEX,{"derivedFrom":[subQ1,subQ0]});Q18=makeQuery(id+"F0.imprint","IMPRINT",FACE,{"disambiguationData":[TD([[makeQuery(id+"F0.imprint","IMPRINT",EDGE,{"disambiguationData":[TD([[subQ2,-1.0]])],"derivedFrom":subQ1}),-1.0]])]});}
            var Q19;
            {var subQ0=sQuery(id+"F0.wireOp",EDGE,"E17.bottom");var subQ1=sQuery(id+"F0.wireOp",EDGE,"E0.right");var subQ2=makeQuery(id+"F0.imprint","INTERSECT",VERTEX,{"derivedFrom":[subQ1,subQ0]});Q19=makeQuery(id+"F0.imprint","IMPRINT",FACE,{"disambiguationData":[TD([[makeQuery(id+"F0.imprint","IMPRINT",EDGE,{"disambiguationData":[TD([[subQ2,-1.0]])],"derivedFrom":subQ1}),1.0]])]});}
            var Q20;
            {var subQ0=sQuery(id+"F0.wireOp",EDGE,"E16.bottom");var subQ1=sQuery(id+"F0.wireOp",EDGE,"E2");var subQ2=makeQuery(id+"F0.imprint","INTERSECT",VERTEX,{"derivedFrom":[subQ1,subQ0]});Q20=makeQuery(id+"F0.imprint","IMPRINT",FACE,{"disambiguationData":[TD([[makeQuery(id+"F0.imprint","IMPRINT",EDGE,{"disambiguationData":[TD([[subQ2,-1.0]])],"derivedFrom":subQ1}),-1.0]])]});}
            var Q21;
            {var subQ6=sQuery(id+"F0.wireOp",EDGE,"E0.top");var subQ11=sQuery(id+"F0.wireOp",EDGE,"E0.left");var subQ12=makeQuery(id+"F0.imprint","INTERSECT",VERTEX,{"derivedFrom":[subQ6,subQ11]});Q21=makeQuery(id+"F0.imprint","IMPRINT",FACE,{"disambiguationData":[TD([[makeQuery(id+"F0.imprint","IMPRINT",EDGE,{"disambiguationData":[TD([[subQ12,-1.0]])],"derivedFrom":subQ6}),-1.0]])]});}
            var Q22;
            {var subQ0=sQuery(id+"F0.wireOp",EDGE,"E20");var subQ1=sQuery(id+"F0.wireOp",EDGE,"E3");var subQ2=makeQuery(id+"F0.imprint","INTERSECT",VERTEX,{"derivedFrom":[subQ1,subQ0]});Q22=makeQuery(id+"F0.imprint","IMPRINT",FACE,{"disambiguationData":[TD([[makeQuery(id+"F0.imprint","IMPRINT",EDGE,{"disambiguationData":[TD([[subQ2,-1.0]])],"derivedFrom":subQ1}),-1.0]])]});}
            var Q23;
            {var subQ0=sQuery(id+"F0.wireOp",EDGE,"E16.right");var subQ1=sQuery(id+"F0.wireOp",EDGE,"E16.top");var subQ2=makeQuery(id+"F0.imprint","INTERSECT",VERTEX,{"derivedFrom":[subQ1,subQ0]});Q23=makeQuery(id+"F0.imprint","IMPRINT",FACE,{"disambiguationData":[TD([[makeQuery(id+"F0.imprint","IMPRINT",EDGE,{"disambiguationData":[TD([[subQ2,1.0]])],"derivedFrom":subQ1}),-1.0]])]});}
            var Q24;
            {var subQ1=sQuery(id+"F0.wireOp",EDGE,"E2");var subQ4=sQuery(id+"F0.wireOp",EDGE,"E3");var subQ5=makeQuery(id+"F0.imprint","INTERSECT",VERTEX,{"derivedFrom":[subQ1,subQ4]});Q24=makeQuery(id+"F0.imprint","IMPRINT",FACE,{"disambiguationData":[TD([[makeQuery(id+"F0.imprint","IMPRINT",EDGE,{"disambiguationData":[TD([[subQ5,1.0]])],"derivedFrom":subQ1}),-1.0]])]});}
            var Q25;
            {var subQ0=sQuery(id+"F0.wireOp",EDGE,"E3");var subQ1=sQuery(id+"F0.wireOp",EDGE,"E2");var subQ2=makeQuery(id+"F0.imprint","INTERSECT",VERTEX,{"derivedFrom":[subQ1,subQ0]});Q25=makeQuery(id+"F0.imprint","IMPRINT",FACE,{"disambiguationData":[TD([[makeQuery(id+"F0.imprint","IMPRINT",EDGE,{"disambiguationData":[TD([[subQ2,1.0]])],"derivedFrom":subQ1}),1.0]])]});}
            extrude(context, id + "F3", {"entities" : qUnion([Q0, Q1, Q2, Q3, Q4, Q5, Q6, Q7, Q8, Q9, Q10, Q11, Q12, Q13, Q14, Q15, Q16, Q17, Q18, Q19, Q20, Q21, Q22, Q23, Q24, Q25]), "operationType" : NewBodyOperationType.ADD, "oppositeDirection" : true, "depth" : 7.8 * mm, "offsetDistance" : 25 * mm});
        }
        {
            var Q0;
            Q0=qCreatedBy(makeId("Top.planeOp"),FACE);
            cPlane(context, id + "F4", {"entities" : qUnion([Q0]), "cplaneType" : CPlaneType.OFFSET, "offset" : 0 * mm, "width" : 150 * mm, "height" : 150 * mm});
        }
        {
            var Q0;
            Q0=qCreatedBy(id+"F4.planeOp",FACE);
            var sketch = newSketch(context, id + "F5", { "sketchPlane" : qUnion([Q0])});
            skPoint(sketch, "E32.0", {"position": v(14.18, 11.5) * mm});
            skPoint(sketch, "E33.0", {"position": v(14.18, -30.2) * mm});
            skPoint(sketch, "E34.0", {"position": v(-15.77, -30.45) * mm});
            skPoint(sketch, "E35.0", {"position": v(-15.77, 11.25) * mm});
            skCircle(sketch, "E36", {"center": v(-15.77, 11.25) * mm, "radius": 0.9 * mm});
            skCircle(sketch, "E37", {"center": v(-15.77, -30.45) * mm, "radius": 0.9 * mm});
            skCircle(sketch, "E38", {"center": v(14.18, -30.2) * mm, "radius": 0.9 * mm});
            skCircle(sketch, "E39", {"center": v(14.18, 11.5) * mm, "radius": 0.9 * mm});
            skSolve(sketch);
        }
        {
            var Q0;
            Q0=makeQuery(id+"F5.imprint","IMPRINT",FACE,{"disambiguationData":[TD([[makeQuery(id+"F5.imprint","IMPRINT",EDGE,{"derivedFrom":sQuery(id+"F5.wireOp",EDGE,"E39")}),1.0]])]});
            var Q1;
            Q1=makeQuery(id+"F5.imprint","IMPRINT",FACE,{"disambiguationData":[TD([[makeQuery(id+"F5.imprint","IMPRINT",EDGE,{"derivedFrom":sQuery(id+"F5.wireOp",EDGE,"E38")}),1.0]])]});
            var Q2;
            Q2=makeQuery(id+"F5.imprint","IMPRINT",FACE,{"disambiguationData":[TD([[makeQuery(id+"F5.imprint","IMPRINT",EDGE,{"derivedFrom":sQuery(id+"F5.wireOp",EDGE,"E37")}),1.0]])]});
            var Q3;
            Q3=makeQuery(id+"F5.imprint","IMPRINT",FACE,{"disambiguationData":[TD([[makeQuery(id+"F5.imprint","IMPRINT",EDGE,{"derivedFrom":sQuery(id+"F5.wireOp",EDGE,"E36")}),1.0]])]});
            extrude(context, id + "F6", {"entities" : qUnion([Q0, Q1, Q2, Q3]), "operationType" : NewBodyOperationType.REMOVE, "oppositeDirection" : true, "depth" : 8 * mm, "offsetDistance" : 25 * mm});
        }
        {
            var Q0;
            Q0=qCreatedBy(makeId("Top.planeOp"),FACE);
            cPlane(context, id + "F7", {"entities" : qUnion([Q0]), "cplaneType" : CPlaneType.OFFSET, "offset" : 10 * mm, "width" : 150 * mm, "height" : 150 * mm});
        }
        {
            var Q0;
            Q0=qCreatedBy(id+"F7.planeOp",FACE);
            var sketch = newSketch(context, id + "F8", { "sketchPlane" : qUnion([Q0])});
            skPoint(sketch, "E40.0", {"position": v(14.18, 11.5) * mm});
            skPoint(sketch, "E41.0", {"position": v(-15.77, 11.25) * mm});
            skPoint(sketch, "E42.0", {"position": v(-15.77, -30.45) * mm});
            skPoint(sketch, "E43.0", {"position": v(14.18, -30.2) * mm});
            skLineSegment(sketch, "E44.0", {"start": v(-18.77, 14.75) * mm, "end": v(-18.77, -33.45) * mm});
            skLineSegment(sketch, "E45.0", {"start": v(-18.77, -33.45) * mm, "end": v(17.43, -33.45) * mm});
            skLineSegment(sketch, "E46.0", {"start": v(17.43, -33.45) * mm, "end": v(17.43, 14.75) * mm});
            skLineSegment(sketch, "E47.0", {"start": v(-13.77, 14.75) * mm, "end": v(-18.77, 14.75) * mm});
            skLineSegment(sketch, "E48.0", {"start": v(17.43, 14.75) * mm, "end": v(10.93, 14.75) * mm});
            skLineSegment(sketch, "E49.0", {"start": v(-1.77, 31.75) * mm, "end": v(-3.27, 31.75) * mm});
            skLineSegment(sketch, "E50.0", {"start": v(-13.77, 14.75) * mm, "end": v(-13.77, 14.75) * mm});
            skLineSegment(sketch, "E51.bottom", {"start": v(7.93, -26.45) * mm, "end": v(12.43, -26.45) * mm});
            skLineSegment(sketch, "E51.top", {"start": v(7.93, 6.55) * mm, "end": v(12.43, 6.55) * mm});
            skLineSegment(sketch, "E51.left", {"start": v(7.93, -26.45) * mm, "end": v(7.93, 6.55) * mm});
            skLineSegment(sketch, "E51.right", {"start": v(12.43, -26.45) * mm, "end": v(12.43, 6.55) * mm});
            skLineSegment(sketch, "E52.bottom", {"start": v(4.93, -26.45) * mm, "end": v(0.43, -26.45) * mm});
            skLineSegment(sketch, "E52.top", {"start": v(4.93, 6.55) * mm, "end": v(0.43, 6.55) * mm});
            skLineSegment(sketch, "E52.left", {"start": v(4.93, -26.45) * mm, "end": v(4.93, 6.55) * mm});
            skLineSegment(sketch, "E52.right", {"start": v(0.43, -26.45) * mm, "end": v(0.43, 6.55) * mm});
            skLineSegment(sketch, "E53.bottom", {"start": v(-2.57, 6.55) * mm, "end": v(-7.07, 6.55) * mm});
            skLineSegment(sketch, "E53.top", {"start": v(-2.57, -26.45) * mm, "end": v(-7.07, -26.45) * mm});
            skLineSegment(sketch, "E53.left", {"start": v(-2.57, 6.55) * mm, "end": v(-2.57, -26.45) * mm});
            skLineSegment(sketch, "E53.right", {"start": v(-7.07, 6.55) * mm, "end": v(-7.07, -26.45) * mm});
            skLineSegment(sketch, "E54.bottom", {"start": v(-10.07, -26.45) * mm, "end": v(-14.57, -26.45) * mm});
            skLineSegment(sketch, "E54.top", {"start": v(-10.07, 6.55) * mm, "end": v(-14.57, 6.55) * mm});
            skLineSegment(sketch, "E54.left", {"start": v(-10.07, -26.45) * mm, "end": v(-10.07, 6.55) * mm});
            skLineSegment(sketch, "E54.right", {"start": v(-14.57, -26.45) * mm, "end": v(-14.57, 6.55) * mm});
            skCircle(sketch, "E55", {"center": v(14.18, -30.2) * mm, "radius": 1.05 * mm});
            skCircle(sketch, "E56", {"center": v(-15.77, -30.45) * mm, "radius": 1.05 * mm});
            skCircle(sketch, "E57", {"center": v(-15.77, 11.25) * mm, "radius": 1.05 * mm});
            skCircle(sketch, "E58", {"center": v(14.18, 11.5) * mm, "radius": 1.05 * mm});
            skLineSegment(sketch, "E59", {"start": v(-13.77, 14.75) * mm, "end": v(10.93, 14.75) * mm});
            skSolve(sketch);
        }
        {
            var Q0;
            Q0=makeQuery(id+"F8.imprint","IMPRINT",FACE,{"disambiguationData":[TD([[makeQuery(id+"F8.imprint","IMPRINT",EDGE,{"derivedFrom":sQuery(id+"F8.wireOp",EDGE,"E44.0")}),1.0]])]});
            extrude(context, id + "F9", {"entities" : qUnion([Q0]), "depth" : 1.5 * mm, "offsetDistance" : 25 * mm});
        }
        {
            var Q0;
            Q0=makeQuery(id+"F9.opExtrude","CAP_EDGE",EDGE,{"disambiguationData":[OSD([sQuery(id+"F8.wireOp",EDGE,"E51.left")])],"isStart":true});
            var Q1;
            Q1=makeQuery(id+"F9.opExtrude","CAP_EDGE",EDGE,{"disambiguationData":[OSD([sQuery(id+"F8.wireOp",EDGE,"E52.right")])],"isStart":true});
            var Q2;
            Q2=makeQuery(id+"F9.opExtrude","CAP_EDGE",EDGE,{"disambiguationData":[OSD([sQuery(id+"F8.wireOp",EDGE,"E53.right")])],"isStart":true});
            var Q3;
            Q3=makeQuery(id+"F9.opExtrude","CAP_EDGE",EDGE,{"disambiguationData":[OSD([sQuery(id+"F8.wireOp",EDGE,"E54.right")])],"isStart":true});
            chamfer(context, id + "F10", {"entities" : qUnion([Q0, Q1, Q2, Q3]), "width" : 1 * mm, "tangentPropagation" : true});
        }
    });
